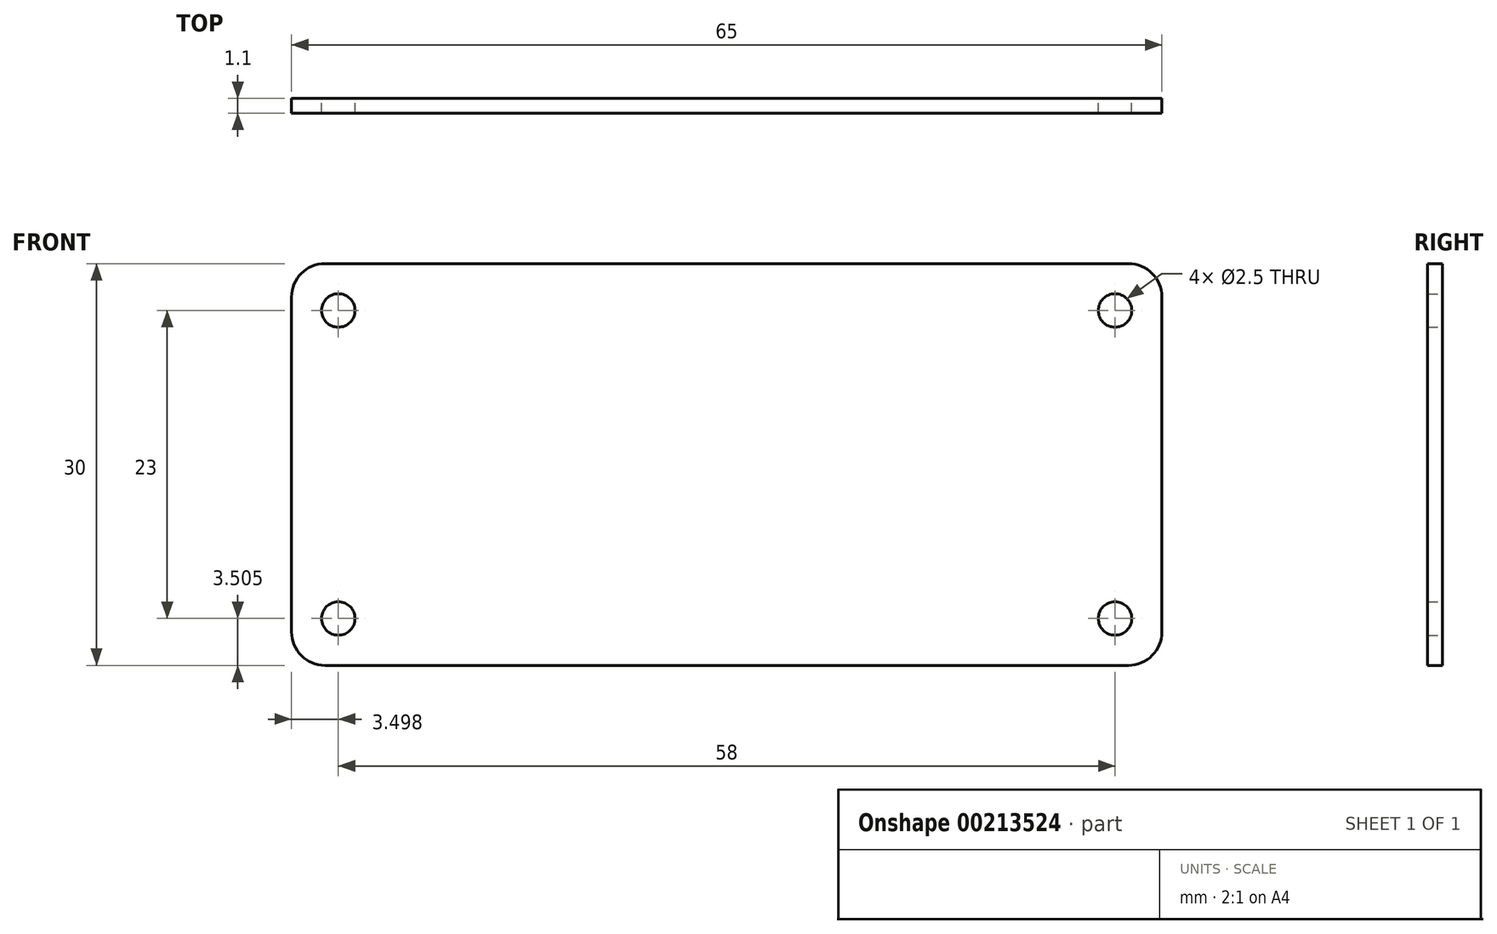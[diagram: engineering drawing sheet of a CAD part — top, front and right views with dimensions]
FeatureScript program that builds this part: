
annotation { "Feature Type Name" : "Feature", "Feature Type Description" : "" }
export const myFeature = defineFeature(function(context is Context, id is Id, definition is map)
    precondition{}
    {
        {
            var Q0;
            Q0=qCreatedBy(makeId("Front.planeOp"),FACE);
            var sketch = newSketch(context, id + "F0", { "sketchPlane" : qUnion([Q0])});
            skLineSegment(sketch, "E0", {"start": v(-28.78, -14.45) * mm, "end": v(31.22, -14.45) * mm});
            skLineSegment(sketch, "E1", {"start": v(33.72, -11.95) * mm, "end": v(33.72, 13.05) * mm});
            skLineSegment(sketch, "E2", {"start": v(31.22, 15.55) * mm, "end": v(-28.78, 15.55) * mm});
            skLineSegment(sketch, "E3", {"start": v(-31.28, 13.05) * mm, "end": v(-31.28, -11.95) * mm});
            skPoint(sketch, "E4.visualSharp", {"position": v(-31.28, 15.55) * mm});
            skArc(sketch, "E4.filletArc", {"start": v(-28.78, 15.55) * mm, "mid": v(-30.55, 14.82) * mm, "end": v(-31.28, 13.05) * mm});
            skPoint(sketch, "E5.visualSharp", {"position": v(-31.28, -14.45) * mm});
            skArc(sketch, "E5.filletArc", {"start": v(-31.28, -11.95) * mm, "mid": v(-30.55, -13.71) * mm, "end": v(-28.78, -14.45) * mm});
            skPoint(sketch, "E6.visualSharp", {"position": v(33.72, -14.45) * mm});
            skArc(sketch, "E6.filletArc", {"start": v(31.22, -14.45) * mm, "mid": v(32.99, -13.71) * mm, "end": v(33.72, -11.95) * mm});
            skPoint(sketch, "E7.visualSharp", {"position": v(33.72, 15.55) * mm});
            skArc(sketch, "E7.filletArc", {"start": v(33.72, 13.05) * mm, "mid": v(32.99, 14.82) * mm, "end": v(31.22, 15.55) * mm});
            skLineSegment(sketch, "E8", {"start": v(33.72, 15.55) * mm, "end": v(33.72, 12.05) * mm, "construction": true});
            skLineSegment(sketch, "E9", {"start": v(33.72, 15.55) * mm, "end": v(30.22, 15.55) * mm, "construction": true});
            skLineSegment(sketch, "E10", {"start": v(30.22, 15.55) * mm, "end": v(30.22, -48.7) * mm, "construction": true});
            skLineSegment(sketch, "E11", {"start": v(33.72, 12.05) * mm, "end": v(-65.25, 12.05) * mm, "construction": true});
            skCircle(sketch, "E12", {"center": v(30.22, 12.05) * mm, "radius": 1.25 * mm});
            skLineSegment(sketch, "E13", {"start": v(33.72, -14.45) * mm, "end": v(33.72, -10.95) * mm, "construction": true});
            skLineSegment(sketch, "E14", {"start": v(33.72, -10.95) * mm, "end": v(-67.48, -10.95) * mm, "construction": true});
            skCircle(sketch, "E15", {"center": v(30.22, -10.95) * mm, "radius": 1.25 * mm});
            skLineSegment(sketch, "E16", {"start": v(30.22, -10.95) * mm, "end": v(-27.78, -10.95) * mm, "construction": true});
            skLineSegment(sketch, "E17", {"start": v(-27.78, -10.95) * mm, "end": v(-27.78, 8.06) * mm, "construction": true});
            skLineSegment(sketch, "E18", {"start": v(-27.78, 8.06) * mm, "end": v(-27.78, -31.4) * mm, "construction": true});
            skCircle(sketch, "E19", {"center": v(-27.78, -10.95) * mm, "radius": 1.25 * mm});
            skCircle(sketch, "E20", {"center": v(-27.78, 12.05) * mm, "radius": 1.25 * mm});
            skLineSegment(sketch, "E21", {"start": v(-28.78, 15.55) * mm, "end": v(-28.78, 13.32) * mm, "construction": true});
            skLineSegment(sketch, "E22", {"start": v(-31.27, 13.32) * mm, "end": v(-22.87, 13.32) * mm, "construction": true});
            skLineSegment(sketch, "E23.0", {"start": v(-6.28, -23.79) * mm, "end": v(-6.28, -3.79) * mm, "construction": true});
            skSolve(sketch);
        }
        {
            var Q0;
            Q0=makeQuery(id+"F0.imprint","IMPRINT",FACE,{"disambiguationData":[TD([[makeQuery(id+"F0.imprint","IMPRINT",EDGE,{"derivedFrom":sQuery(id+"F0.wireOp",EDGE,"E0")}),1.0]])]});
            extrude(context, id + "F1", {"entities" : qUnion([Q0]), "depth" : 1.1 * mm});
        }
    });
